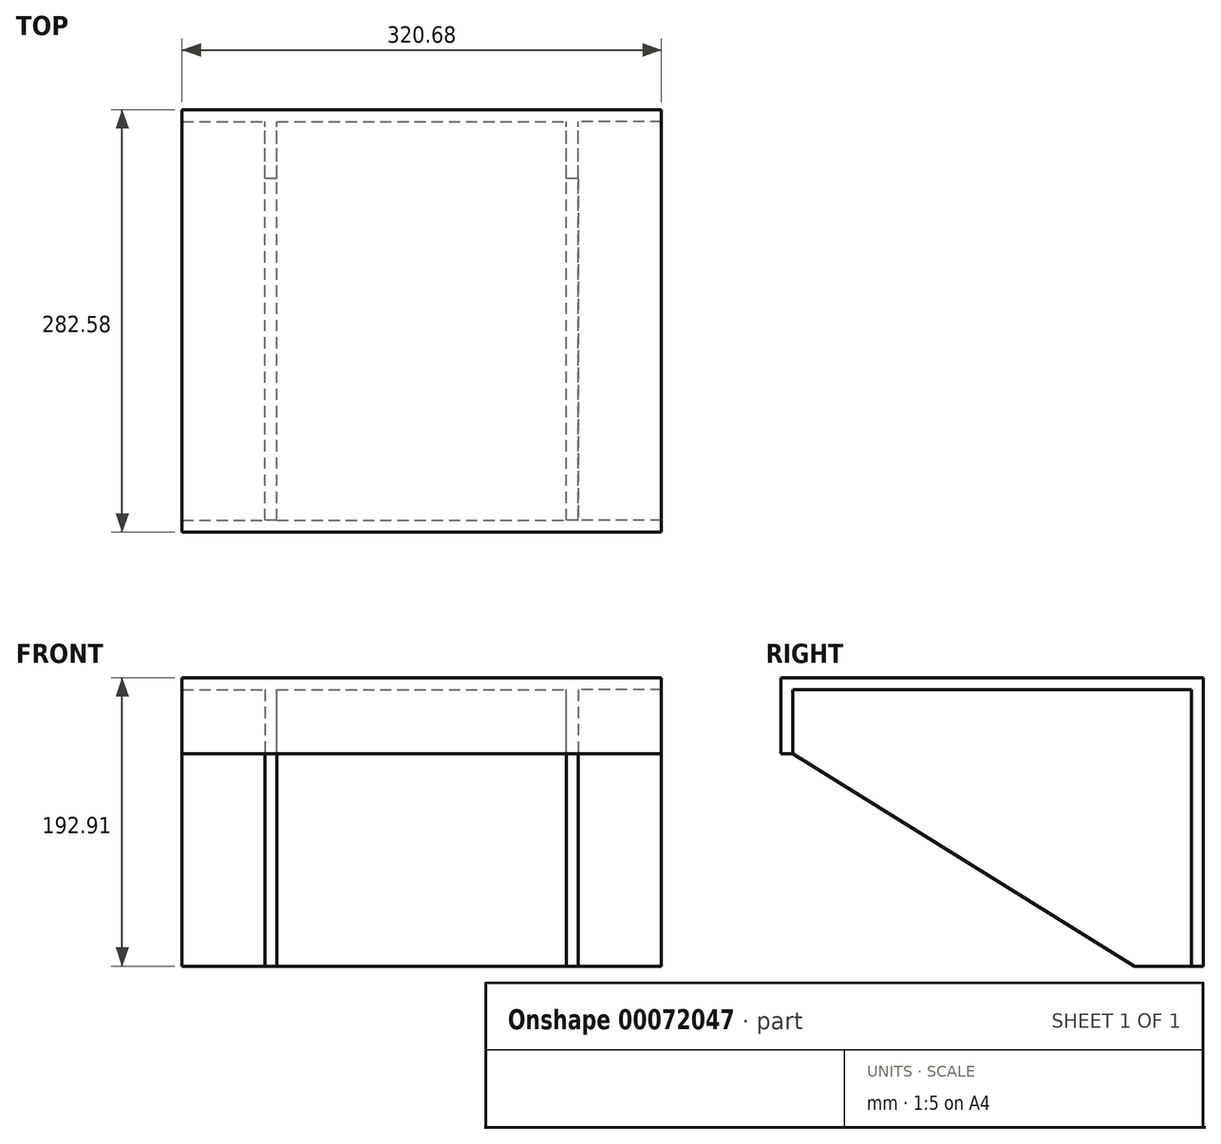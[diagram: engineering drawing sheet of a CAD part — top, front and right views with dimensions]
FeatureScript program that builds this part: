
annotation { "Feature Type Name" : "Feature", "Feature Type Description" : "" }
export const myFeature = defineFeature(function(context is Context, id is Id, definition is map)
    precondition{}
    {
        {
            var Q0;
            Q0=qCreatedBy(makeId("Front.planeOp"),FACE);
            var sketch = newSketch(context, id + "F0", { "sketchPlane" : qUnion([Q0])});
            skLineSegment(sketch, "E0.bottom", {"start": v(-160.34, 0) * mm, "end": v(160.34, 0) * mm});
            skLineSegment(sketch, "E0.top", {"start": v(-160.34, -192.91) * mm, "end": v(160.34, -192.91) * mm});
            skLineSegment(sketch, "E0.left", {"start": v(-160.34, 0) * mm, "end": v(-160.34, -192.91) * mm});
            skLineSegment(sketch, "E0.right", {"start": v(160.34, 0) * mm, "end": v(160.34, -192.91) * mm});
            skSolve(sketch);
        }
        {
            var Q0;
            Q0=makeQuery(id+"F0.imprint","IMPRINT",FACE,{"disambiguationData":[TD([[makeQuery(id+"F0.imprint","IMPRINT",EDGE,{"derivedFrom":sQuery(id+"F0.wireOp",EDGE,"E0.bottom")}),-1.0]])]});
            extrude(context, id + "F1", {"entities" : qUnion([Q0]), "depth" : 7.94 * mm});
        }
        {
            var Q0;
            Q0=makeQuery(id+"F1.opExtrude","CAP_FACE",FACE,{"disambiguationData":[OSD([sQuery(id+"F0.wireOp",EDGE,"E0.bottom"),sQuery(id+"F0.wireOp",EDGE,"E0.top"),sQuery(id+"F0.wireOp",EDGE,"E0.left"),sQuery(id+"F0.wireOp",EDGE,"E0.right")])],"isStart":false});
            var sketch = newSketch(context, id + "F2", { "sketchPlane" : qUnion([Q0])});
            skLineSegment(sketch, "E1.bottom", {"start": v(-131.76, -110.36) * mm, "end": v(131.76, -110.36) * mm});
            skLineSegment(sketch, "E1.top", {"start": v(-131.76, -173.86) * mm, "end": v(131.76, -173.86) * mm});
            skLineSegment(sketch, "E1.left", {"start": v(-131.76, -110.36) * mm, "end": v(-131.76, -173.86) * mm});
            skLineSegment(sketch, "E1.right", {"start": v(131.76, -110.36) * mm, "end": v(131.76, -173.86) * mm});
            skSolve(sketch);
        }
        {
            var Q0;
            Q0=makeQuery(id+"F1.opExtrude","CAP_FACE",FACE,{"disambiguationData":[OSD([sQuery(id+"F0.wireOp",EDGE,"E0.bottom"),sQuery(id+"F0.wireOp",EDGE,"E0.top"),sQuery(id+"F0.wireOp",EDGE,"E0.left"),sQuery(id+"F0.wireOp",EDGE,"E0.right")])],"isStart":false});
            var sketch = newSketch(context, id + "F3", { "sketchPlane" : qUnion([Q0])});
            skLineSegment(sketch, "E2", {"start": v(-160.34, 0) * mm, "end": v(-160.34, -7.94) * mm});
            skLineSegment(sketch, "E3", {"start": v(-160.34, -7.94) * mm, "end": v(-104.78, -7.94) * mm});
            skLineSegment(sketch, "E4", {"start": v(-104.78, -7.94) * mm, "end": v(-104.78, -192.91) * mm});
            skLineSegment(sketch, "E5", {"start": v(-104.78, -192.91) * mm, "end": v(-96.84, -192.91) * mm});
            skLineSegment(sketch, "E6", {"start": v(-96.84, -192.91) * mm, "end": v(-96.84, -7.94) * mm});
            skLineSegment(sketch, "E7.MirrorCS", {"start": v(160.34, -7.94) * mm, "end": v(104.78, -7.94) * mm});
            skLineSegment(sketch, "E8.MirrorCS", {"start": v(96.84, -192.91) * mm, "end": v(96.84, -7.94) * mm});
            skLineSegment(sketch, "E9.MirrorCS", {"start": v(104.78, -7.94) * mm, "end": v(104.78, -192.91) * mm});
            skLineSegment(sketch, "E10.MirrorCS", {"start": v(104.78, -192.91) * mm, "end": v(96.84, -192.91) * mm});
            skLineSegment(sketch, "E11.MirrorCS", {"start": v(160.34, 0) * mm, "end": v(160.34, -7.94) * mm});
            skLineSegment(sketch, "E12", {"start": v(-96.84, -7.94) * mm, "end": v(96.84, -7.94) * mm});
            skLineSegment(sketch, "E13", {"start": v(-160.34, 0) * mm, "end": v(160.34, 0) * mm});
            skSolve(sketch);
        }
        {
            var Q0;
            Q0=qSketchRegion(id+"F3",true);
            extrude(context, id + "F4", {"entities" : qUnion([Q0]), "operationType" : NewBodyOperationType.ADD, "depth" : 266.7 * mm});
        }
        {
            var Q0;
            Q0=makeQuery(id+"F4.opExtrude","SWEPT_FACE",FACE,{"disambiguationData":[OSD([sQuery(id+"F3.wireOp",EDGE,"E4")])]});
            var sketch = newSketch(context, id + "F5", { "sketchPlane" : qUnion([Q0])});
            skLineSegment(sketch, "E14", {"start": v(46.04, -192.91) * mm, "end": v(274.64, -192.91) * mm});
            skLineSegment(sketch, "E15", {"start": v(274.64, -192.91) * mm, "end": v(274.64, -50.8) * mm});
            skLineSegment(sketch, "E16", {"start": v(274.64, -50.8) * mm, "end": v(46.04, -192.91) * mm});
            skSolve(sketch);
        }
        {
            var Q0;
            Q0=qSketchRegion(id+"F5",true);
            extrude(context, id + "F6", {"entities" : qUnion([Q0]), "operationType" : NewBodyOperationType.REMOVE, "endBound" : BoundingType.THROUGH_ALL, "oppositeDirection" : true, "depth" : 25.4 * mm});
        }
        {
            var Q0;
            Q0=makeQuery(id+"F4.boolean.opBoolean","MERGE",FACE,{"derivedFrom":[makeQuery(id+"F1.opExtrude","SWEPT_FACE",FACE,{"disambiguationData":[OSD([sQuery(id+"F0.wireOp",EDGE,"E0.bottom")])]}),makeQuery(id+"F4.opExtrude","SWEPT_FACE",FACE,{"disambiguationData":[OSD([sQuery(id+"F3.wireOp",EDGE,"E13")])]})]});
            var sketch = newSketch(context, id + "F7", { "sketchPlane" : qUnion([Q0])});
            skLineSegment(sketch, "E17.bottom", {"start": v(-75.97, -138.85) * mm, "end": v(24.03, -138.85) * mm});
            skLineSegment(sketch, "E17.top", {"start": v(-75.97, -238.85) * mm, "end": v(24.03, -238.85) * mm});
            skLineSegment(sketch, "E17.left", {"start": v(-75.97, -138.85) * mm, "end": v(-75.97, -238.85) * mm});
            skLineSegment(sketch, "E17.right", {"start": v(24.03, -138.85) * mm, "end": v(24.03, -238.85) * mm});
            skSolve(sketch);
        }
        {
            var Q0;
            Q0=makeQuery(id+"F4.opExtrude","CAP_FACE",FACE,{"disambiguationData":[OSD([sQuery(id+"F3.wireOp",EDGE,"E2"),sQuery(id+"F3.wireOp",EDGE,"E3"),sQuery(id+"F3.wireOp",EDGE,"E4"),sQuery(id+"F3.wireOp",EDGE,"E5"),sQuery(id+"F3.wireOp",EDGE,"E6"),sQuery(id+"F3.wireOp",EDGE,"E7.MirrorCS"),sQuery(id+"F3.wireOp",EDGE,"E8.MirrorCS"),sQuery(id+"F3.wireOp",EDGE,"E9.MirrorCS"),sQuery(id+"F3.wireOp",EDGE,"E10.MirrorCS"),sQuery(id+"F3.wireOp",EDGE,"E11.MirrorCS"),sQuery(id+"F3.wireOp",EDGE,"E12"),sQuery(id+"F3.wireOp",EDGE,"E13")])],"isStart":false});
            var sketch = newSketch(context, id + "F8", { "sketchPlane" : qUnion([Q0])});
            skLineSegment(sketch, "E18.bottom", {"start": v(-160.34, 0) * mm, "end": v(160.34, 0) * mm});
            skLineSegment(sketch, "E18.top", {"start": v(-160.34, -50.8) * mm, "end": v(160.34, -50.8) * mm});
            skLineSegment(sketch, "E18.left", {"start": v(-160.34, 0) * mm, "end": v(-160.34, -50.8) * mm});
            skLineSegment(sketch, "E18.right", {"start": v(160.34, 0) * mm, "end": v(160.34, -50.8) * mm});
            skSolve(sketch);
        }
        {
            var Q0;
            Q0 = qSketchRegion(id + "F8", true);
            extrude(context, id + "F9", {"entities" : qUnion([Q0]), "operationType" : NewBodyOperationType.ADD, "depth" : 7.94 * mm});
        }
    });
